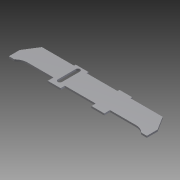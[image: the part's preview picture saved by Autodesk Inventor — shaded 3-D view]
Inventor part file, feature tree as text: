
AUTODESK INVENTOR PART (.ipt)
format: ipt  version: 2011 (Build 150239000, 239)  size: 121,344 bytes
history: native  units: mm
features: extrude x2, sketch x2, other x1
ambient origin geometry x8: Origin, YZ Plane, XZ Plane, XY Plane, X Axis, Y Axis, Z Axis, Center Point
feature tree (5):
  other  "Sólido1"
  extrude  "Extrusión1"  Depth=5.0mm
  extrude  "Extrusión2"  Depth=6.7mm
  sketch  "Boceto1"  dims[d0=18.0mm d1=5.0mm]
  sketch  "Boceto2"  dims[d2=15.0mm d3=6.7mm d4=31.0mm d5=15.0mm d6=10.0mm d7=4.5mm d8=6.5mm d9=12.5mm d12=2.3mm d13=15.0mm d14=2.0mm d15=37.5mm d17=24.0mm d18=2.0mm d19=0.0mm d20=23.5mm d21=5.0mm d22=26.0mm d24=2.5mm d25=10.0mm d26=0.0mm]
